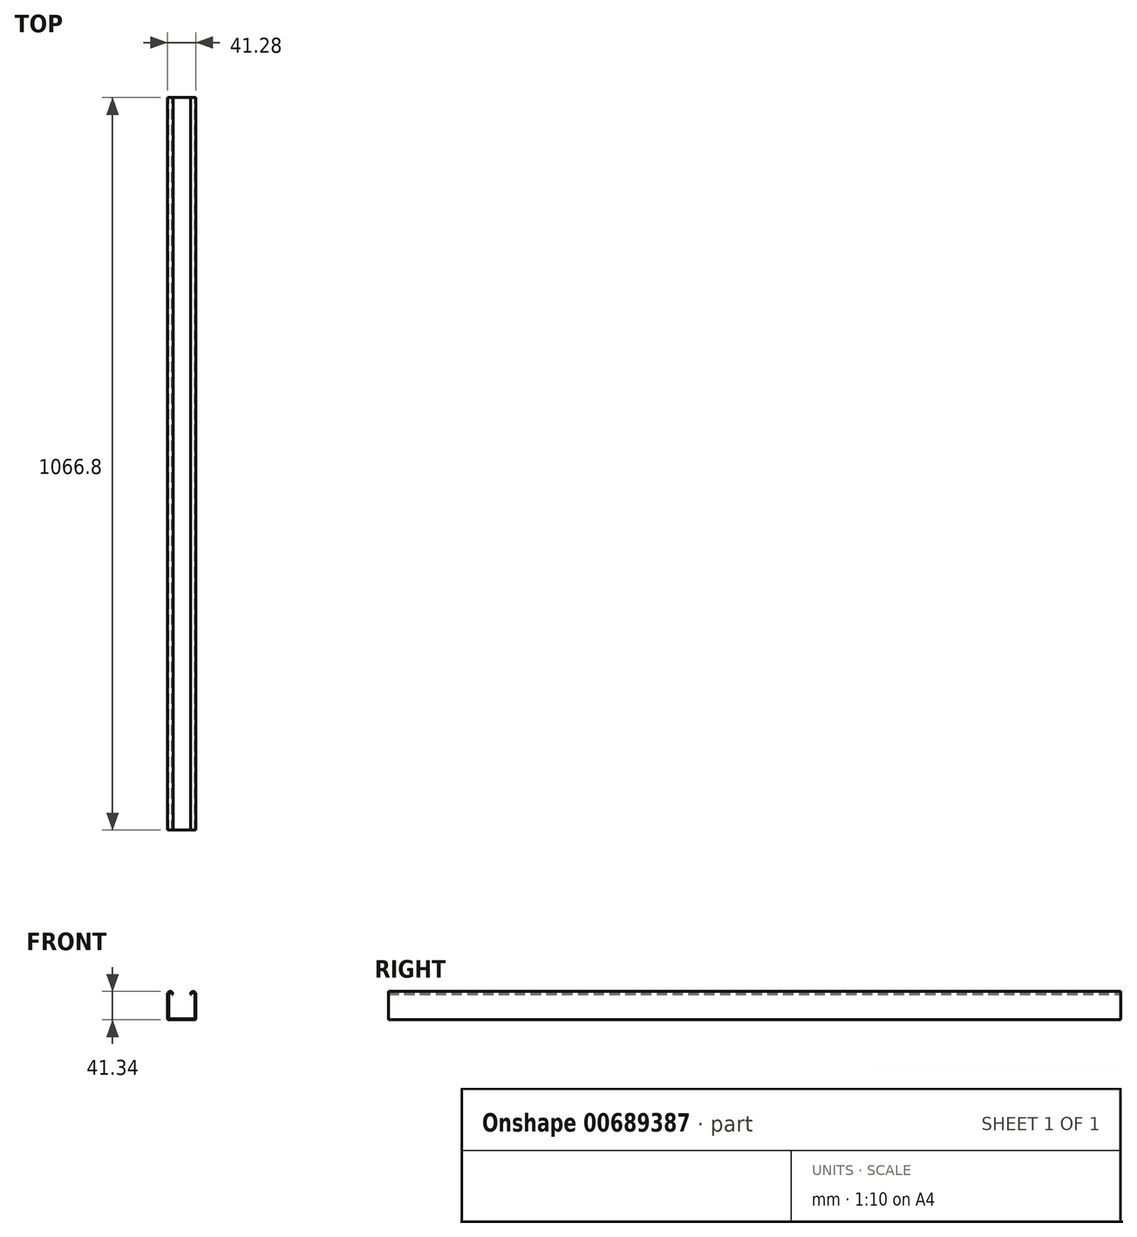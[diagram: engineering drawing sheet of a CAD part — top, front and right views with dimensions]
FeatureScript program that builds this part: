
annotation { "Feature Type Name" : "Feature", "Feature Type Description" : "" }
export const myFeature = defineFeature(function(context is Context, id is Id, definition is map)
    precondition{}
    {
        {
            var Q0;
            Q0=qCreatedBy(makeId("Front.planeOp"),FACE);
            var sketch = newSketch(context, id + "F0", { "sketchPlane" : qUnion([Q0])});
            skLineSegment(sketch, "E0.bottom", {"start": v(20.64, -20.64) * mm, "end": v(-20.64, -20.64) * mm});
            skLineSegment(sketch, "E0.top", {"start": v(17.36, 20.64) * mm, "end": v(15.98, 20.64) * mm});
            skLineSegment(sketch, "E0.left", {"start": v(20.64, -20.64) * mm, "end": v(20.64, 16.73) * mm});
            skLineSegment(sketch, "E0.right", {"start": v(-20.64, -20.64) * mm, "end": v(-20.64, 16.73) * mm});
            skPoint(sketch, "E0.middle", {"position": v(0, 0) * mm});
            skLineSegment(sketch, "E1.0", {"start": v(-19.05, -20.64) * mm, "end": v(-19.05, 16.73) * mm});
            skLineSegment(sketch, "E2.0", {"start": v(20.64, -19.05) * mm, "end": v(-20.64, -19.05) * mm});
            skLineSegment(sketch, "E3.0", {"start": v(19.05, -20.64) * mm, "end": v(19.05, 16.73) * mm});
            skArc(sketch, "E4", {"start": v(-12.7, 16.73) * mm, "mid": v(-16.67, 20.7) * mm, "end": v(-20.64, 16.73) * mm});
            skArc(sketch, "E5", {"start": v(-14.29, 16.73) * mm, "mid": v(-16.67, 19.11) * mm, "end": v(-19.05, 16.73) * mm});
            skArc(sketch, "E6.MirrorC", {"start": v(12.7, 16.73) * mm, "mid": v(16.67, 20.7) * mm, "end": v(20.64, 16.73) * mm});
            skArc(sketch, "E7.MirrorC", {"start": v(14.29, 16.73) * mm, "mid": v(16.67, 19.11) * mm, "end": v(19.05, 16.73) * mm});
            skPoint(sketch, "E8.orphan", {"position": v(-20.64, 20.64) * mm});
            skLineSegment(sketch, "E9.trimOffspring", {"start": v(-15.98, 20.64) * mm, "end": v(-17.36, 20.64) * mm});
            skLineSegment(sketch, "E10.trimOffspring", {"start": v(-14.29, 16.73) * mm, "end": v(-12.7, 16.73) * mm});
            skLineSegment(sketch, "E11.trimOffspring", {"start": v(12.7, 16.73) * mm, "end": v(14.29, 16.73) * mm});
            skPoint(sketch, "E12.orphan", {"position": v(20.64, 20.64) * mm});
            skSolve(sketch);
        }
        {
            var Q0;
            Q0 = qSketchRegion(id + "F0", true);
            extrude(context, id + "F1", {"entities" : qUnion([Q0]), "depth" : 1066.8 * mm, "offsetDistance" : 25.4 * mm});
        }
        {
            var Q0;
            Q0=makeQuery(id+"F1.opExtrude","SWEPT_EDGE",EDGE,{"disambiguationData":[OSD([sQuery(id+"F0.wireOp",EDGE,"E1.0"),sQuery(id+"F0.wireOp",EDGE,"E2.0")])]});
            var Q1;
            Q1=makeQuery(id+"F1.opExtrude","SWEPT_EDGE",EDGE,{"disambiguationData":[OSD([sQuery(id+"F0.wireOp",EDGE,"E2.0"),sQuery(id+"F0.wireOp",EDGE,"E3.0")])]});
            var Q2;
            Q2=makeQuery(id+"F1.opExtrude","SWEPT_EDGE",EDGE,{"disambiguationData":[OSD([sQuery(id+"F0.wireOp",EDGE,"E0.bottom"),sQuery(id+"F0.wireOp",EDGE,"E0.left")])]});
            var Q3;
            Q3=makeQuery(id+"F1.opExtrude","SWEPT_EDGE",EDGE,{"disambiguationData":[OSD([sQuery(id+"F0.wireOp",EDGE,"E0.bottom"),sQuery(id+"F0.wireOp",EDGE,"E0.right")])]});
            fillet(context, id + "F2", {"entities" : qUnion([Q0, Q1, Q2, Q3]), "radius" : 1.59 * mm, "tangentPropagation" : true, "allowEdgeOverflow" : false});
        }
    });
